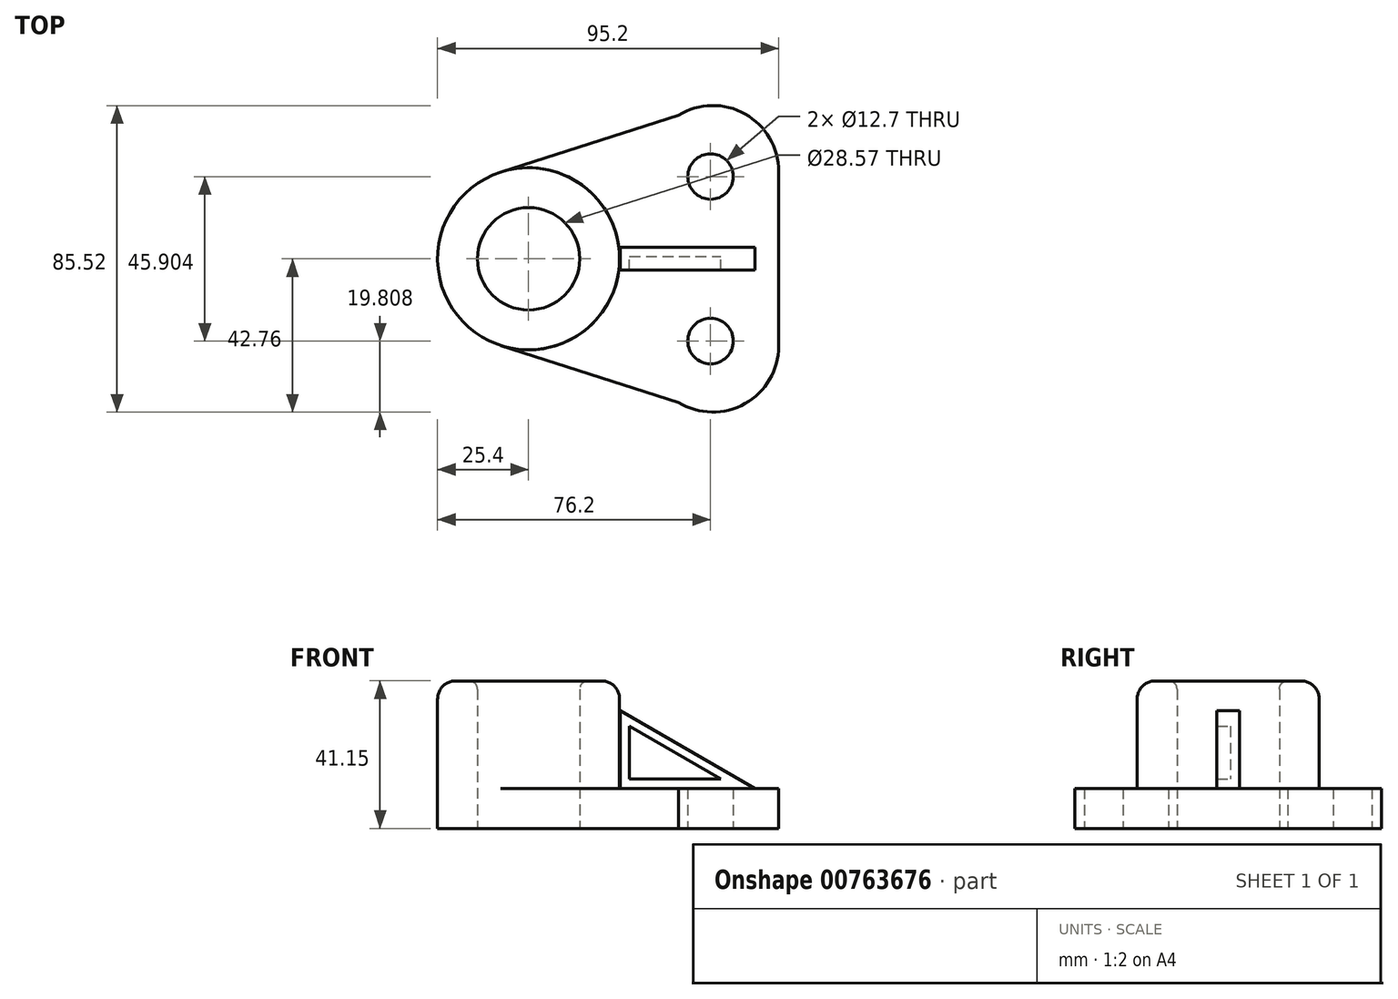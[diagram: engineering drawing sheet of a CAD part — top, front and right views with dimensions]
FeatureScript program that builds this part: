
annotation { "Feature Type Name" : "Feature", "Feature Type Description" : "" }
export const myFeature = defineFeature(function(context is Context, id is Id, definition is map)
    precondition{}
    {
        {
            var Q0;
            Q0=qCreatedBy(makeId("Top.planeOp"),FACE);
            var sketch = newSketch(context, id + "F0", { "sketchPlane" : qUnion([Q0])});
            skLineSegment(sketch, "E0", {"start": v(0, -3.9) * mm, "end": v(0, -22.95) * mm, "construction": true});
            skArc(sketch, "E1", {"start": v(19, -24.37) * mm, "mid": v(19.05, -22.95) * mm, "end": v(19, -21.54) * mm});
            skCircle(sketch, "E2", {"center": v(0, -22.95) * mm, "radius": 6.35 * mm});
            skLineSegment(sketch, "E3", {"start": v(0, -22.95) * mm, "end": v(-6.35, -22.95) * mm, "construction": true});
            skLineSegment(sketch, "E4", {"start": v(-50.8, -22.95) * mm, "end": v(-50.8, 0) * mm, "construction": true});
            skCircle(sketch, "E5", {"center": v(-50.8, 0) * mm, "radius": 25.4 * mm});
            skCircle(sketch, "E6", {"center": v(-50.8, 0) * mm, "radius": 14.29 * mm});
            skLineSegment(sketch, "E7", {"start": v(-58.55, -24.19) * mm, "end": v(-8.94, -40.1) * mm});
            skPoint(sketch, "E8.end.orphan", {"position": v(-8.94, 51.02) * mm});
            skPoint(sketch, "E8.start.orphan", {"position": v(-58.55, 24.19) * mm});
            skPoint(sketch, "E9.orphan", {"position": v(0, 34.2) * mm});
            skLineSegment(sketch, "E10", {"start": v(19, -24.37) * mm, "end": v(19, 0) * mm});
            skLineSegment(sketch, "E11", {"start": v(19, 0) * mm, "end": v(-25.4, 0) * mm});
            skArc(sketch, "E12", {"start": v(-8.94, -40.1) * mm, "mid": v(9.62, -40.4) * mm, "end": v(19, -24.37) * mm});
            skSolve(sketch);
        }
        {
            var Q0;
            Q0=makeQuery(id+"F0.imprint","IMPRINT",FACE,{"disambiguationData":[TD([[makeQuery(id+"F0.imprint","IMPRINT",EDGE,{"derivedFrom":sQuery(id+"F0.wireOp",EDGE,"E6")}),-1.0]])]});
            extrude(context, id + "F1", {"entities" : qUnion([Q0]), "depth" : 41.15 * mm, "offsetDistance" : 25.4 * mm});
        }
        {
            var Q0;
            Q0=makeQuery(id+"F0.imprint","IMPRINT",FACE,{"disambiguationData":[TD([[makeQuery(id+"F0.imprint","IMPRINT",EDGE,{"derivedFrom":sQuery(id+"F0.wireOp",EDGE,"E2")}),-1.0]])]});
            extrude(context, id + "F2", {"entities" : qUnion([Q0]), "operationType" : NewBodyOperationType.ADD, "depth" : 11.18 * mm, "offsetDistance" : 25.4 * mm});
        }
        {
            var Q0;
            Q0=makeQuery(id+"F2.opExtrude","CAP_FACE",FACE,{"disambiguationData":[OSD([sQuery(id+"F0.wireOp",EDGE,"E2"),sQuery(id+"F0.wireOp",EDGE,"E5"),sQuery(id+"F0.wireOp",EDGE,"E7"),sQuery(id+"F0.wireOp",EDGE,"E10"),sQuery(id+"F0.wireOp",EDGE,"E11"),sQuery(id+"F0.wireOp",EDGE,"E12")])],"isStart":false});
            var sketch = newSketch(context, id + "F3", { "sketchPlane" : qUnion([Q0])});
            skPoint(sketch, "E13.0", {"position": v(-25.4, 0) * mm});
            skLineSegment(sketch, "E14.0", {"start": v(19, 0) * mm, "end": v(-25.4, 0) * mm});
            skCircle(sketch, "E15.0", {"center": v(-50.8, 0) * mm, "radius": 25.4 * mm});
            skLineSegment(sketch, "E16", {"start": v(19, 0) * mm, "end": v(15.7, 0) * mm, "construction": true});
            skLineSegment(sketch, "E17", {"start": v(15.7, 0) * mm, "end": v(-25.4, 0) * mm});
            skLineSegment(sketch, "E18", {"start": v(-25.4, 0) * mm, "end": v(15.7, 0) * mm});
            skSolve(sketch);
        }
        {
            var Q0;
            Q0 = qSketchRegion(id + "F3", true);
            extrude(context, id + "F4", {"entities" : qUnion([Q0]), "operationType" : NewBodyOperationType.ADD, "depth" : 25.4 * mm, "offsetDistance" : 25.4 * mm});
        }
        {
            var sketch = newSketch(context, id + "F5", { "sketchPlane" : qUnion([])});
            skLineSegment(sketch, "E19", {"start": v(0, 41.4) * mm, "end": v(0, 11.3) * mm});
            skSolve(sketch);
        }
        {
            var Q0;
            Q0=makeQuery(id+"F3.imprint","IMPRINT",FACE,{"disambiguationData":[TD([[makeQuery(id+"F3.imprint","IMPRINT",EDGE,{"derivedFrom":sQuery(id+"F3.wireOp",EDGE,"E14.0")}),1.0]])]});
            var sketch = newSketch(context, id + "F6", { "sketchPlane" : qUnion([Q0])});
            skLineSegment(sketch, "E20", {"start": v(-25.41, 0) * mm, "end": v(15.71, 0) * mm});
            skSolve(sketch);
        }
        {
            var Q0;
            Q0=makeQuery(id+"F1.opExtrude","SWEPT_BODY",BODY,{"disambiguationData":[OSD([sQuery(id+"F0.wireOp",EDGE,"E5"),sQuery(id+"F0.wireOp",EDGE,"E6")])]});
            var Q1;
            Q1=qCreatedBy(makeId("Front.planeOp"),FACE);
            mirror(context, id + "F7", {"operationType" : NewBodyOperationType.ADD, "entities" : qUnion([Q0]), "mirrorPlane" : qUnion([Q1])});
        }
        {
            var Q0;
            Q0=makeQuery(id+"F4.opExtrude","CAP_FACE",FACE,{"disambiguationData":[OSD([sQuery(id+"F3.wireOp",EDGE,"E15.0")])],"isStart":false});
            extrude(context, id + "F8", {"entities" : qUnion([Q0]), "operationType" : NewBodyOperationType.REMOVE, "endBound" : BoundingType.THROUGH_ALL, "oppositeDirection" : true, "depth" : 25.4 * mm, "offsetDistance" : 25.4 * mm});
        }
        {
            var Q0;
            Q0=qCreatedBy(makeId("Front.planeOp"),FACE);
            var sketch = newSketch(context, id + "F9", { "sketchPlane" : qUnion([Q0])});
            skLineSegment(sketch, "E21.0", {"start": v(-25.15, 41.4) * mm, "end": v(-25.15, 11.3) * mm});
            skLineSegment(sketch, "E22.0", {"start": v(-25.41, 11.18) * mm, "end": v(15.71, 11.18) * mm});
            skLineSegment(sketch, "E23", {"start": v(-25.15, 32.86) * mm, "end": v(12.41, 11.18) * mm});
            skLineSegment(sketch, "E24", {"start": v(-25.15, 32.86) * mm, "end": v(-25.15, 11.3) * mm});
            skLineSegment(sketch, "E25", {"start": v(12.41, 11.18) * mm, "end": v(-25.15, 11.3) * mm});
            skSolve(sketch);
        }
        {
            var Q0;
            Q0=makeQuery(id+"F1.opExtrude","CAP_EDGE",EDGE,{"disambiguationData":[OSD([sQuery(id+"F0.wireOp",EDGE,"E5")])],"isStart":false});
            var Q1;
            {var subQ0=makeQuery(id+"F2.opExtrude","CAP_EDGE",EDGE,{"disambiguationData":[OSD([sQuery(id+"F0.wireOp",EDGE,"E5")])],"isStart":false});Q1=makeQuery(id+"F7.boolean.opBoolean","MERGE",EDGE,{"derivedFrom":[subQ0,makeQuery(id+"F7.opPattern","COPY",EDGE,{"derivedFrom":subQ0,"instanceName":"1"})]});}
            fillet(context, id + "F10", {"entities" : qUnion([Q0, Q1]), "radius" : 5.08 * mm, "tangentPropagation" : true, "allowEdgeOverflow" : false});
        }
        {
            var Q0;
            {var subQ0=sQuery(id+"F9.wireOp",EDGE,"E23");Q0=makeQuery(id+"F9.imprint","IMPRINT",FACE,{"disambiguationData":[TD([[makeQuery(id+"F9.imprint","IMPRINT",EDGE,{"derivedFrom":subQ0}),-1.0]])]});}
            extrude(context, id + "F11", {"entities" : qUnion([Q0]), "depth" : 3.17 * mm, "offsetDistance" : 25.4 * mm, "hasSecondDirection" : true, "secondDirectionOppositeDirection" : true, "secondDirectionDepth" : 3.17 * mm});
        }
        {
            var Q0;
            Q0=makeQuery(id+"F11.opExtrude","CAP_FACE",FACE,{"disambiguationData":[OSD([sQuery(id+"F9.wireOp",EDGE,"E21.0"),sQuery(id+"F9.wireOp",EDGE,"E23"),sQuery(id+"F9.wireOp",EDGE,"E25")])],"isStart":false});
            shell(context, id + "F12", {"entities" : qUnion([Q0]), "thickness" : 2.54 * mm});
        }
        {
            var Q0;
            Q0=makeQuery(id+"F1.opExtrude","CAP_EDGE",EDGE,{"disambiguationData":[OSD([sQuery(id+"F0.wireOp",EDGE,"E6")])],"isStart":false});
            fillet(context, id + "F13", {"entities" : qUnion([Q0]), "radius" : 2.3 * mm, "tangentPropagation" : true, "allowEdgeOverflow" : false});
        }
    });
